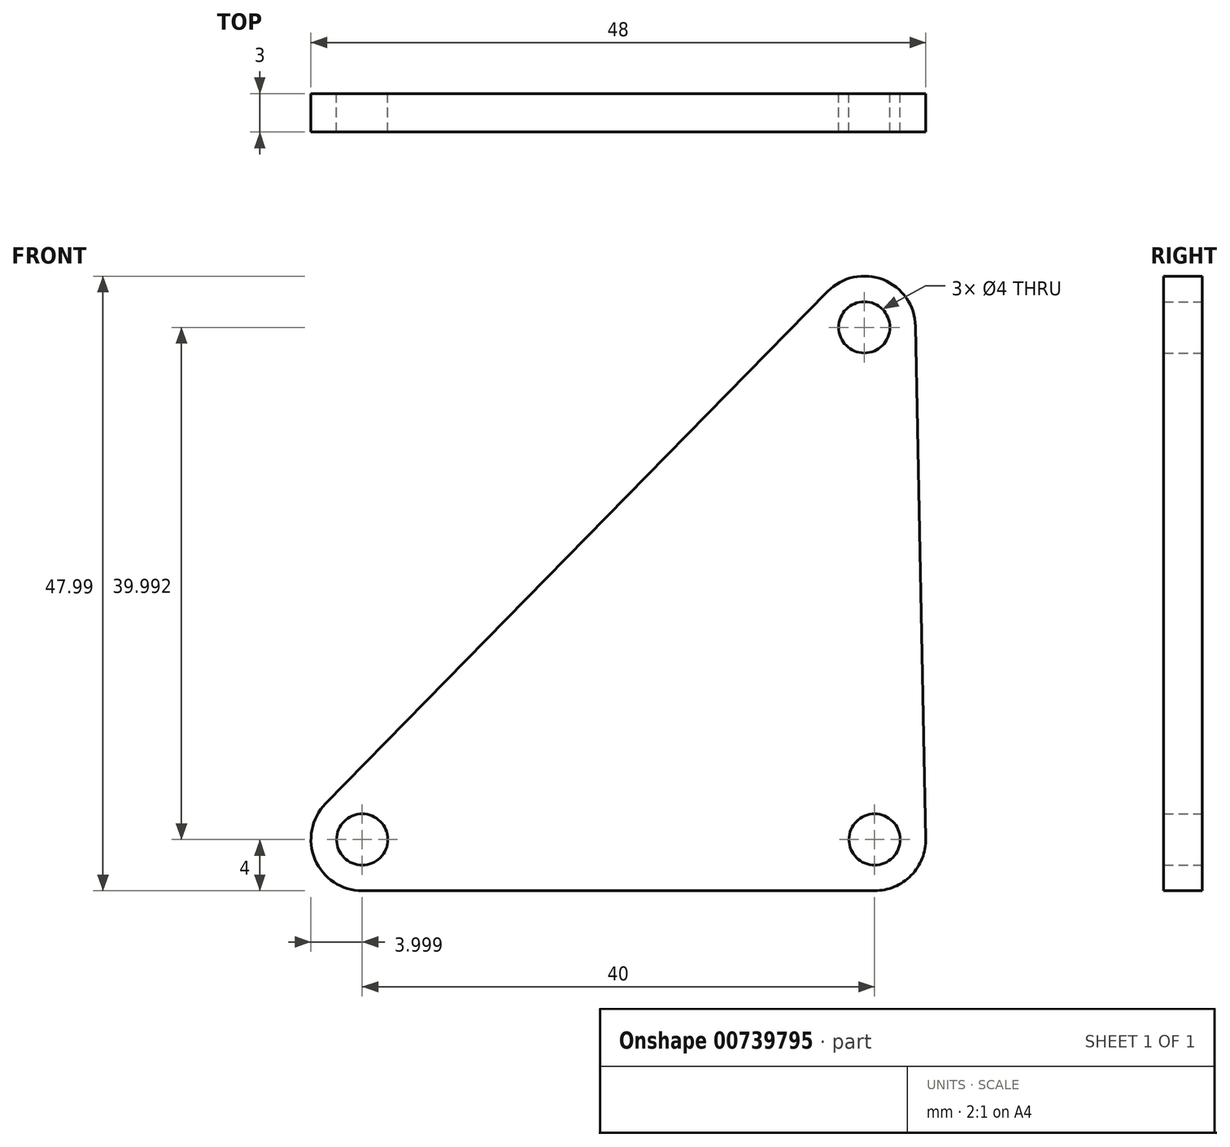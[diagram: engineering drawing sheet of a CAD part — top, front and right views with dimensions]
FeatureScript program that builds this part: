
annotation { "Feature Type Name" : "Feature", "Feature Type Description" : "" }
export const myFeature = defineFeature(function(context is Context, id is Id, definition is map)
    precondition{}
    {
        {
            var Q0;
            Q0=qCreatedBy(makeId("Front.planeOp"),FACE);
            var sketch = newSketch(context, id + "F0", { "sketchPlane" : qUnion([Q0])});
            skLineSegment(sketch, "E0", {"start": v(-0.08, 4.08) * mm, "end": v(-0.88, 44.07) * mm});
            skLineSegment(sketch, "E1", {"start": v(-7.74, 46.8) * mm, "end": v(-46.94, 6.8) * mm});
            skLineSegment(sketch, "E2", {"start": v(-44.08, 0) * mm, "end": v(-4.08, 0) * mm});
            skPoint(sketch, "E3.visualSharp", {"position": v(-1.07, 53.6) * mm});
            skArc(sketch, "E3.filletArc", {"start": v(-0.88, 44.07) * mm, "mid": v(-3.4, 47.71) * mm, "end": v(-7.74, 46.8) * mm});
            skPoint(sketch, "E4.visualSharp", {"position": v(-53.6, 0) * mm});
            skArc(sketch, "E4.filletArc", {"start": v(-46.94, 6.8) * mm, "mid": v(-47.77, 2.45) * mm, "end": v(-44.08, 0) * mm});
            skPoint(sketch, "E5.visualSharp", {"position": v(0, 0) * mm});
            skArc(sketch, "E5.filletArc", {"start": v(-4.08, 0) * mm, "mid": v(-1.22, 1.2) * mm, "end": v(-0.08, 4.08) * mm});
            skCircle(sketch, "E6", {"center": v(-44.08, 4) * mm, "radius": 2 * mm});
            skCircle(sketch, "E7", {"center": v(-4.08, 4) * mm, "radius": 2 * mm});
            skCircle(sketch, "E8", {"center": v(-4.88, 44) * mm, "radius": 2 * mm});
            skSolve(sketch);
        }
        {
            var Q0;
            Q0 = qSketchRegion(id + "F0", true);
            extrude(context, id + "F1", {"entities" : qUnion([Q0]), "depth" : 3 * mm, "offsetDistance" : 25 * mm});
        }
    });
